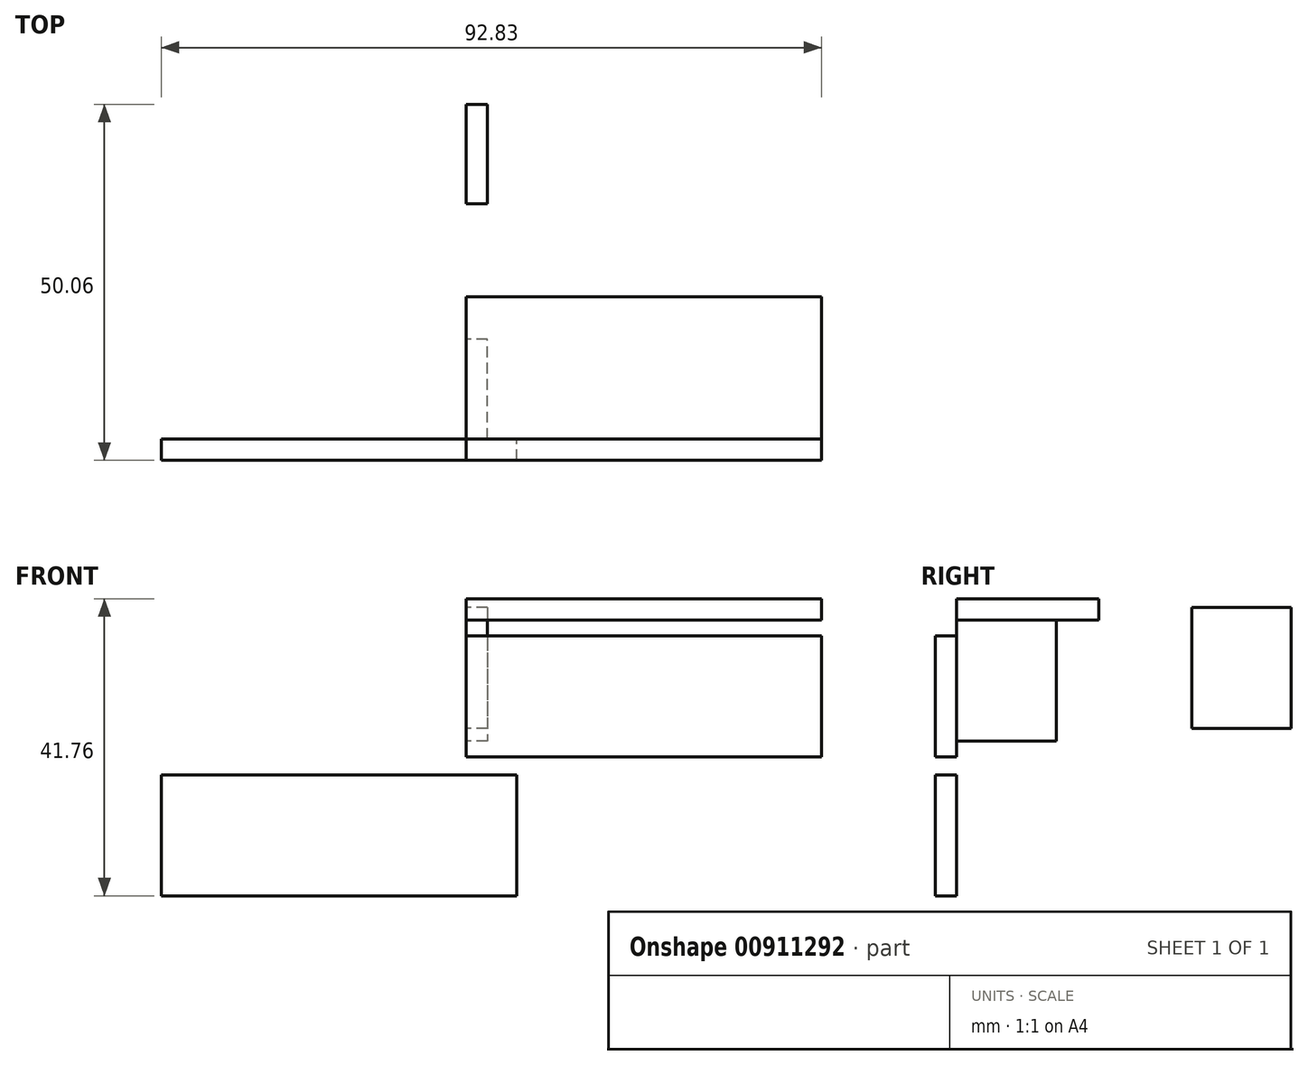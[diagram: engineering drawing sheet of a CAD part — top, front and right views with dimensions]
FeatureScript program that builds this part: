
annotation { "Feature Type Name" : "Feature", "Feature Type Description" : "" }
export const myFeature = defineFeature(function(context is Context, id is Id, definition is map)
    precondition{}
    {
        {
            var Q0;
            Q0=qCreatedBy(makeId("Top.planeOp"),FACE);
            var sketch = newSketch(context, id + "F0", { "sketchPlane" : qUnion([Q0])});
            skLineSegment(sketch, "E0", {"start": v(0, 0) * mm, "end": v(49.2, 0) * mm});
            skLineSegment(sketch, "E1", {"start": v(49.2, 0) * mm, "end": v(-43.24, 173.31) * mm});
            skLineSegment(sketch, "E2", {"start": v(-43.24, 173.31) * mm, "end": v(-95.09, 173.31) * mm});
            skLineSegment(sketch, "E3", {"start": v(-95.09, 173.31) * mm, "end": v(0, 0) * mm});
            skSolve(sketch);
        }
        {
            var Q0;
            Q0=makeQuery(id+"F0.imprint","IMPRINT",FACE,{"disambiguationData":[TD([[makeQuery(id+"F0.imprint","IMPRINT",EDGE,{"derivedFrom":sQuery(id+"F0.wireOp",EDGE,"E0")}),1.0]])]});
            extrude(context, id + "F1", {"entities" : qUnion([Q0]), "oppositeDirection" : true, "depth" : 5.08 * mm, "offsetDistance" : 25.4 * mm});
        }
        {
            var Q0;
            Q0=makeQuery(id+"F1.opExtrude","SWEPT_BODY",BODY,{"disambiguationData":[OSD([sQuery(id+"F0.wireOp",EDGE,"E0"),sQuery(id+"F0.wireOp",EDGE,"E1"),sQuery(id+"F0.wireOp",EDGE,"E2"),sQuery(id+"F0.wireOp",EDGE,"E3")])]});
            deleteBodies(context, id + "F2", {"entities" : qUnion([Q0])});
        }
        {
            var Q0;
            Q0=qCreatedBy(makeId("Top.planeOp"),FACE);
            var sketch = newSketch(context, id + "F3", { "sketchPlane" : qUnion([Q0])});
            skLineSegment(sketch, "E4.bottom", {"start": v(0, 0) * mm, "end": v(50, 0) * mm});
            skLineSegment(sketch, "E4.top", {"start": v(0, 20) * mm, "end": v(50, 20) * mm});
            skLineSegment(sketch, "E4.left", {"start": v(0, 0) * mm, "end": v(0, 20) * mm});
            skLineSegment(sketch, "E4.right", {"start": v(50, 0) * mm, "end": v(50, 20) * mm});
            skSolve(sketch);
        }
        {
            var Q0;
            Q0=makeQuery(id+"F3.imprint","IMPRINT",FACE,{"disambiguationData":[TD([[makeQuery(id+"F3.imprint","IMPRINT",EDGE,{"derivedFrom":sQuery(id+"F3.wireOp",EDGE,"E4.bottom")}),1.0]])]});
            extrude(context, id + "F4", {"entities" : qUnion([Q0]), "depth" : 3 * mm, "offsetDistance" : 25 * mm});
        }
        {
            var Q0;
            Q0=qCreatedBy(makeId("Front.planeOp"),FACE);
            var sketch = newSketch(context, id + "F5", { "sketchPlane" : qUnion([Q0])});
            skLineSegment(sketch, "E5.bottom", {"start": v(0, -2.23) * mm, "end": v(50, -2.23) * mm});
            skLineSegment(sketch, "E5.top", {"start": v(0, -19.23) * mm, "end": v(50, -19.23) * mm});
            skLineSegment(sketch, "E5.left", {"start": v(0, -2.23) * mm, "end": v(0, -19.23) * mm});
            skLineSegment(sketch, "E5.right", {"start": v(50, -2.23) * mm, "end": v(50, -19.23) * mm});
            skSolve(sketch);
        }
        {
            var Q0;
            Q0 = qSketchRegion(id + "F5", true);
            extrude(context, id + "F6", {"entities" : qUnion([Q0]), "depth" : 3 * mm, "offsetDistance" : 25 * mm});
        }
        {
            var Q0;
            Q0=qCreatedBy(makeId("Right.planeOp"),FACE);
            var sketch = newSketch(context, id + "F7", { "sketchPlane" : qUnion([Q0])});
            skLineSegment(sketch, "E6.bottom", {"start": v(0, 0) * mm, "end": v(14, 0) * mm});
            skLineSegment(sketch, "E6.top", {"start": v(0, -17) * mm, "end": v(14, -17) * mm});
            skLineSegment(sketch, "E6.left", {"start": v(0, 0) * mm, "end": v(0, -17) * mm});
            skLineSegment(sketch, "E6.right", {"start": v(14, 0) * mm, "end": v(14, -17) * mm});
            skSolve(sketch);
        }
        {
            var Q0;
            Q0=makeQuery(id+"F7.imprint","IMPRINT",FACE,{"disambiguationData":[TD([[makeQuery(id+"F7.imprint","IMPRINT",EDGE,{"derivedFrom":sQuery(id+"F7.wireOp",EDGE,"E6.bottom")}),-1.0]])]});
            extrude(context, id + "F8", {"entities" : qUnion([Q0]), "depth" : 3 * mm, "offsetDistance" : 25 * mm});
        }
        {
            var Q0;
            Q0=qCreatedBy(makeId("Right.planeOp"),FACE);
            var sketch = newSketch(context, id + "F9", { "sketchPlane" : qUnion([Q0])});
            skLineSegment(sketch, "E7.bottom", {"start": v(33.06, 1.77) * mm, "end": v(47.06, 1.77) * mm});
            skLineSegment(sketch, "E7.top", {"start": v(33.06, -15.23) * mm, "end": v(47.06, -15.23) * mm});
            skLineSegment(sketch, "E7.left", {"start": v(33.06, 1.77) * mm, "end": v(33.06, -15.23) * mm});
            skLineSegment(sketch, "E7.right", {"start": v(47.06, 1.77) * mm, "end": v(47.06, -15.23) * mm});
            skSolve(sketch);
        }
        {
            var Q0;
            Q0 = qSketchRegion(id + "F9", true);
            extrude(context, id + "F10", {"entities" : qUnion([Q0]), "depth" : 3 * mm, "offsetDistance" : 25 * mm});
        }
        {
            var Q0;
            Q0=qCreatedBy(makeId("Front.planeOp"),FACE);
            var sketch = newSketch(context, id + "F11", { "sketchPlane" : qUnion([Q0])});
            skLineSegment(sketch, "E8.bottom", {"start": v(7.17, -38.76) * mm, "end": v(-42.83, -38.76) * mm});
            skLineSegment(sketch, "E8.top", {"start": v(7.17, -21.76) * mm, "end": v(-42.83, -21.76) * mm});
            skLineSegment(sketch, "E8.left", {"start": v(7.17, -38.76) * mm, "end": v(7.17, -21.76) * mm});
            skLineSegment(sketch, "E8.right", {"start": v(-42.83, -38.76) * mm, "end": v(-42.83, -21.76) * mm});
            skSolve(sketch);
        }
        {
            var Q0;
            Q0 = qSketchRegion(id + "F11", true);
            var Q1;
            Q1=makeQuery(id+"F11.imprint","IMPRINT",FACE,{"disambiguationData":[TD([[makeQuery(id+"F11.imprint","IMPRINT",EDGE,{"derivedFrom":sQuery(id+"F11.wireOp",EDGE,"E8.bottom")}),-1.0]])]});
            extrude(context, id + "F12", {"entities" : qUnion([Q0, Q1]), "depth" : 3 * mm, "offsetDistance" : 25 * mm});
        }
    });
